# Revit family: Bernhardt_Design-Tables-Conference-Playbook_Lounge_Y-base
name_source: partatom
category: Furniture
revit_build: Autodesk Revit 2016 (Build: 20150714_1515(x64)
units: mm (PartAtom-declared; Revit-internal decimal feet)

## family parameters
Always vertical = Yes
Cut with Voids When Loaded = No
OmniClass Number = 23.40.20.00
OmniClass Title = General Furniture and Specialties
Room Calculation Point = No
Shared = No
Work Plane-Based = No

## types (13) — shared parameters
Base variety = det_01
Conference height = No
Manufacturer = Bernhardt Design
Model = Playbook
URL = http://www.bernhardtdesign.com
base_massive_on = No
base_on_second = Yes
base_quant_massive = 2
massive_02_off = No
massive_02_on = Yes
mediafelt_massive_on = No
mediafelt_on_third = No
mediafelt_quantity_massive = 2
null = 0' - 0"

## per-type parameters (varying)
| type | Catalog | Tabletop - curved | Tabletop - restangular | Tabletop curved - variety | Tabletop variety | Tabletop_lenght | Tabletop_width | base_on_first | base_on_third | base_quantity | base_third_corrbias | bias_02 | bias_massive_02 | lenght_02 | mediafelt_on_first | mediafelt_on_one | mediafelt_on_second |
| Playbook - 3 y-bases 120"w x 48"d x 29.5"h radius rect lounge height | PKS-FOC-YL | No | Yes | det_tabletop_curved : Playbook - 2 t-bases 96"w x 48"d x 29.5"h tele conference height | det_tabletop_restangular : Radius restangular | 10' - 0" | 4' - 0" | Yes | Yes | 3 | 0' - 0" | 3' - 2 7/16" | 3' - 2 7/16" | 6' - 4 27/32" | Yes | No | Yes |
| Playbook - 2 y-bases 96"w x 48"d x 29.5"h rect lounge height | PKS-EKC-YL | No | Yes | det_tabletop_curved : Playbook - 2 t-bases 96"w x 48"d x 29.5"h tele conference height | det_tabletop_restangular : Restangular | 7' - 11 31/32" | 4' - 0" | Yes | No | 2 | 0' - 4" | 2' - 2 7/16" | 4' - 4 27/32" | 4' - 4 27/32" | No | Yes | No |
| Playbook - 3 y-bases 120"w x 48"d x 29.5"h rect lounge height | PKS-EOC-YL | No | Yes | det_tabletop_curved : Playbook - 2 t-bases 96"w x 48"d x 29.5"h tele conference height | det_tabletop_restangular : Restangular | 10' - 0" | 4' - 0" | Yes | Yes | 3 | 0' - 0" | 3' - 2 7/16" | 3' - 2 7/16" | 6' - 4 27/32" | Yes | No | Yes |
| Playbook - 1 y-base 48"w x 48"d x 29.5"h runoff lounge height | PKS-MCC-YL | Yes | No | det_tabletop_curved : Playbook - 1 t-base 48"w x 48"d x 29.5"h runoff conference height | det_tabletop_restangular : Restangular | 20' - 0" | 4' - 6 1/32" | No | No | 2 | 0' - 4" | 2' - 1 7/32" | 2' - 9 9/32" | 2' - 9 9/32" | No | Yes | No |
| Playbook - 2 y-bases 96"w x 48"d x 29.5"h radius rect lounge height | PKS-IKC-YL | No | Yes | det_tabletop_curved : Playbook - 2 t-bases 96"w x 48"d x 29.5"h tele conference height | det_tabletop_restangular : Radius restangular | 7' - 11 31/32" | 4' - 0" | Yes | No | 2 | 0' - 4" | 2' - 2 7/16" | 4' - 4 27/32" | 4' - 4 27/32" | No | Yes | No |
| Playbook - 3 y-bases 120"w x 48"d x 29.5"h capsule lounge height | PKS-GOC-YL | Yes | No | det_tabletop_curved : Playbook - 3 t-bases 120"w x 48"d x 29.5"h capsule conference height | det_tabletop_restangular : Restangular | 20' - 0" | 4' - 6 1/32" | Yes | Yes | 3 | 0' - 0" | 3' - 2 7/16" | 3' - 2 7/16" | 6' - 4 29/32" | Yes | No | Yes |
| Playbook - 3 y-bases 120"w x 48"d x 29.5"h tele lounge height | PKS-IOC-YL | Yes | No | det_tabletop_curved : Playbook - 3 t-bases 120"w x 48"d x 29.5"h tele conference height | det_tabletop_restangular : Restangular | 20' - 0" | 4' - 6 1/32" | Yes | Yes | 3 | 0' - 0" | 3' - 2 7/16" | 3' - 2 7/16" | 6' - 4 7/8" | Yes | No | Yes |
| Playbook - 2 y-bases 96"w x 48"d x 29.5"h tele lounge height | PKS-IKC-YL | Yes | No | det_tabletop_curved : Playbook - 2 t-bases 96"w x 48"d x 29.5"h tele conference height | det_tabletop_restangular : Restangular | 20' - 0" | 4' - 6 1/32" | Yes | No | 2 | 0' - 4" | 2' - 2 13/32" | 4' - 4 27/32" | 4' - 4 27/32" | No | Yes | No |
| Playbook - 1 y-base 66"w x 48"d x 29.5"h runoff lounge height | PKS-MFC-YL | Yes | No | det_tabletop_curved : Playbook - 1 t-base 66"w x 48"d x 29.5"h runoff conference height | det_tabletop_restangular : Restangular | 20' - 0" | 4' - 6 1/32" | No | No | 2 | 0' - 4" | 2' - 10 15/32" | 4' - 3 1/4" | 4' - 3 1/4" | No | Yes | No |
| Playbook - 1 y-base 84"w x 48"d x 29.5"h runoff lounge height | PKS-MIC-YL | Yes | No | det_tabletop_curved : Playbook - 1 t-base 84"w x 48"d x 29.5"h runoff conference height | det_tabletop_restangular : Restangular | 20' - 0" | 4' - 6 1/32" | No | No | 2 | 0' - 4" | 3' - 7 9/32" | 5' - 3 3/4" | 5' - 3 3/4" | No | Yes | No |
| Playbook - 2 y-bases 96"w x 48"d x 29.5"h runoff lounge height | PKS-MKC-YL | Yes | No | det_tabletop_curved : Playbook - 2 t-bases 96"w x 48"d x 29.5"h runoff conference height | det_tabletop_restangular : Restangular | 20' - 0" | 4' - 6 1/32" | No | Yes | 3 | 0' - 0" | 4' - 1 9/32" | 3' - 1 27/32" | 6' - 3 23/32" | Yes | No | Yes |
| Playbook - 3 y-bases 120"w x 48"d x 29.5"h runoff lounge height | PKS-MOC-YL | Yes | No | det_tabletop_curved : Playbook - 3 t-bases 120"w x 48"d x 29.5"h runoff conference height | det_tabletop_restangular : Restangular | 20' - 0" | 4' - 6 1/32" | No | Yes | 3 | 0' - 0" | 5' - 1 5/16" | 4' - 1 7/8" | 8' - 3 23/32" | Yes | No | Yes |
| Playbook - 2 y-bases 96"w x 48"d x 29.5"h capsule lounge height | PKS-GKC-YL | Yes | No | det_tabletop_curved : Playbook - 2 t-bases 96"w x 48"d x 29.5"h capsule conference height | det_tabletop_restangular : Restangular | 20' - 0" | 4' - 6 1/32" | Yes | No | 2 | 0' - 4" | 2' - 2 17/32" | 4' - 5 1/32" | 4' - 5 1/32" | No | Yes | No |

## geometry (parser evidence)
native form markers: Sweep x42
no freeform markers — native parametric forms only
